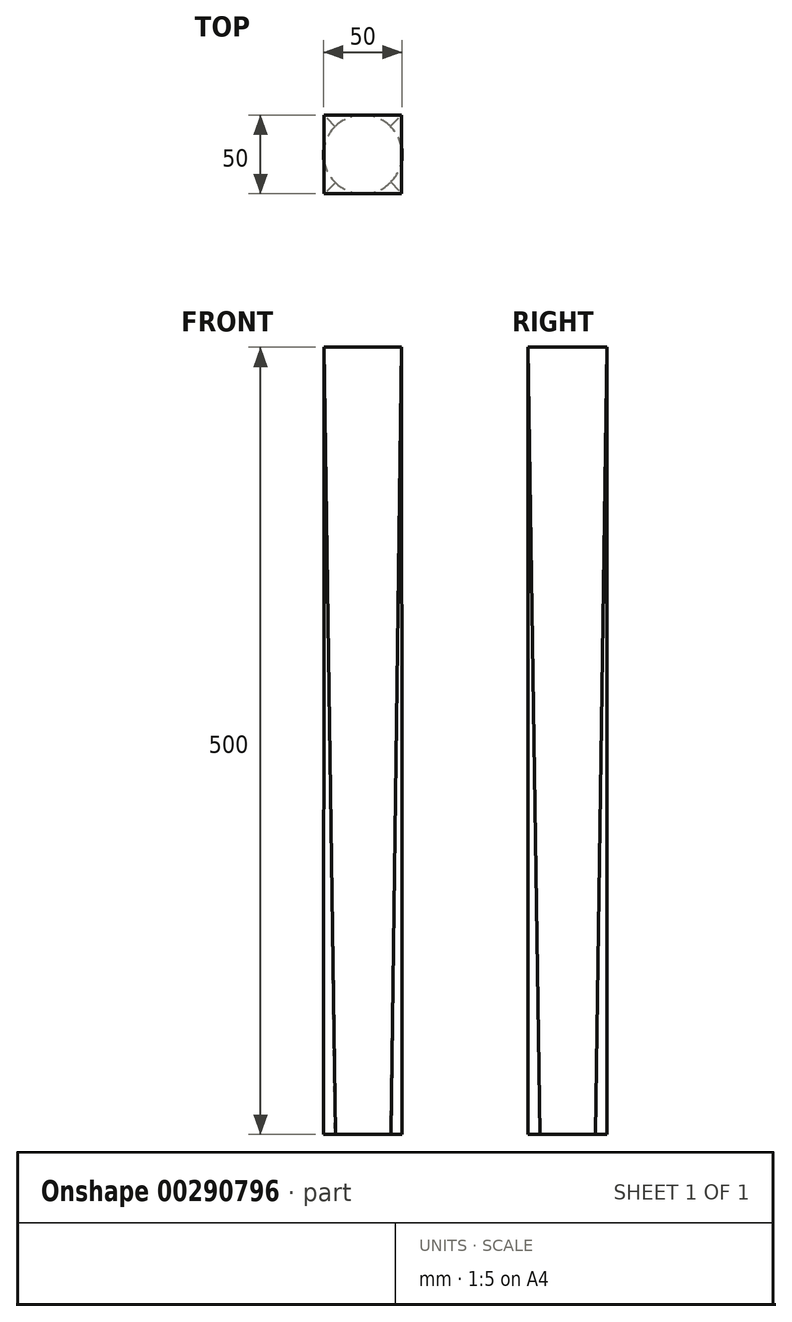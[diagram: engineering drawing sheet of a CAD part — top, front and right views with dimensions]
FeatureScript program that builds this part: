
annotation { "Feature Type Name" : "Feature", "Feature Type Description" : "" }
export const myFeature = defineFeature(function(context is Context, id is Id, definition is map)
    precondition{}
    {
        {
            var Q0;
            Q0=qCreatedBy(makeId("Top.planeOp"),FACE);
            var sketch = newSketch(context, id + "F0", { "sketchPlane" : qUnion([Q0])});
            skLineSegment(sketch, "E0.bottom", {"start": v(-65.06, 24.36) * mm, "end": v(-15.06, 24.36) * mm});
            skLineSegment(sketch, "E0.top", {"start": v(-65.06, -25.64) * mm, "end": v(-15.06, -25.64) * mm});
            skLineSegment(sketch, "E0.left", {"start": v(-65.06, 24.36) * mm, "end": v(-65.06, -25.64) * mm});
            skLineSegment(sketch, "E0.right", {"start": v(-15.06, 24.36) * mm, "end": v(-15.06, -25.64) * mm});
            skSolve(sketch);
        }
        {
            var Q0;
            Q0 = qSketchRegion(id + "F0", true);
            extrude(context, id + "F1", {"entities" : qUnion([Q0]), "depth" : 500 * mm});
        }
        {
            var Q0;
            Q0=makeQuery(id+"F1.opExtrude","SWEPT_BODY",BODY,{"disambiguationData":[OSD([sQuery(id+"F0.wireOp",EDGE,"E0.bottom"),sQuery(id+"F0.wireOp",EDGE,"E0.top"),sQuery(id+"F0.wireOp",EDGE,"E0.left"),sQuery(id+"F0.wireOp",EDGE,"E0.right")])]});
            deleteBodies(context, id + "F2", {"entities" : qUnion([Q0])});
        }
        {
            var Q0;
            Q0=qCreatedBy(makeId("Top.planeOp"),FACE);
            var sketch = newSketch(context, id + "F3", { "sketchPlane" : qUnion([Q0])});
            skCircle(sketch, "E1", {"center": v(0, 0) * mm, "radius": 25 * mm});
            skSolve(sketch);
        }
        {
            var Q0;
            Q0=qCreatedBy(makeId("Top.planeOp"),FACE);
            cPlane(context, id + "F4", {"entities" : qUnion([Q0]), "cplaneType" : CPlaneType.OFFSET, "offset" : 500 * mm, "width" : 150 * mm, "height" : 150 * mm});
        }
        {
            var Q0;
            Q0=qCreatedBy(id+"F4.planeOp",FACE);
            var sketch = newSketch(context, id + "F5", { "sketchPlane" : qUnion([Q0])});
            skLineSegment(sketch, "E2.bottom", {"start": v(24.56, 25) * mm, "end": v(-24.56, 25) * mm});
            skLineSegment(sketch, "E2.top", {"start": v(24.56, -25) * mm, "end": v(-24.56, -25) * mm});
            skLineSegment(sketch, "E2.left", {"start": v(24.56, 25) * mm, "end": v(24.56, -25) * mm});
            skLineSegment(sketch, "E2.right", {"start": v(-24.56, 25) * mm, "end": v(-24.56, -25) * mm});
            skPoint(sketch, "E2.middle", {"position": v(0, 0) * mm});
            skSolve(sketch);
        }
        {
            var Q0;
            Q0=makeQuery(id+"F3.imprint","IMPRINT",FACE,{"disambiguationData":[TD([[makeQuery(id+"F3.imprint","IMPRINT",EDGE,{"derivedFrom":sQuery(id+"F3.wireOp",EDGE,"E1")}),1.0]])]});
            var Q1;
            Q1=makeQuery(id+"F5.imprint","IMPRINT",FACE,{"disambiguationData":[TD([[makeQuery(id+"F5.imprint","IMPRINT",EDGE,{"derivedFrom":sQuery(id+"F5.wireOp",EDGE,"E2.bottom")}),1.0]])]});
            loft(context, id + "F6", {"sheetProfilesArray" : [{ "sheetProfileEntities" : qUnion([Q0]) }, { "sheetProfileEntities" : qUnion([Q1]) }]});
        }
    });
